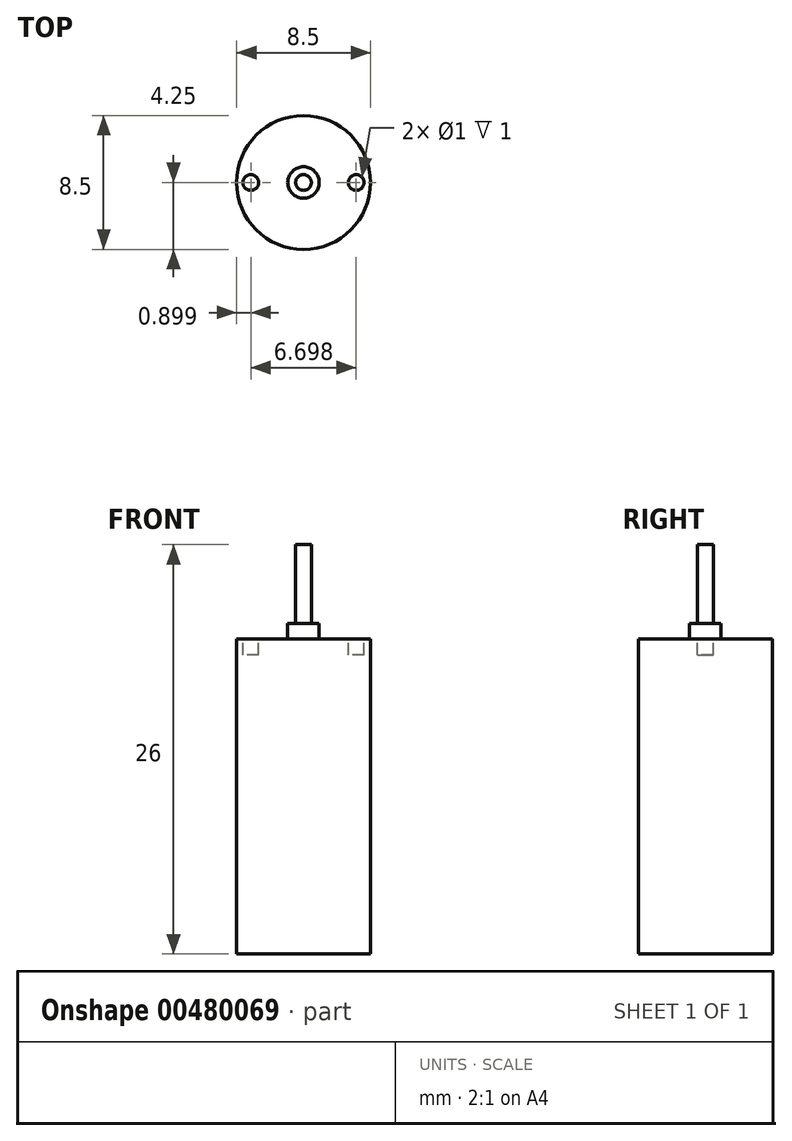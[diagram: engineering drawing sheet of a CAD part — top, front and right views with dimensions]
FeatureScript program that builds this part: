
annotation { "Feature Type Name" : "Feature", "Feature Type Description" : "" }
export const myFeature = defineFeature(function(context is Context, id is Id, definition is map)
    precondition{}
    {
        {
            var Q0;
            Q0=qCreatedBy(makeId("Front.planeOp"),FACE);
            var sketch = newSketch(context, id + "F0", { "sketchPlane" : qUnion([Q0])});
            skLineSegment(sketch, "E0.bottom", {"start": v(-4.64, 12.4) * mm, "end": v(3.86, 12.4) * mm});
            skLineSegment(sketch, "E0.top", {"start": v(-4.64, -7.6) * mm, "end": v(3.86, -7.6) * mm});
            skLineSegment(sketch, "E0.left", {"start": v(-4.64, 12.4) * mm, "end": v(-4.64, -7.6) * mm, "construction": true});
            skLineSegment(sketch, "E0.right", {"start": v(3.86, 12.4) * mm, "end": v(3.86, -7.6) * mm});
            skLineSegment(sketch, "E1.bottom", {"start": v(-0.4, 12.4) * mm, "end": v(-1.4, 12.4) * mm});
            skLineSegment(sketch, "E1.top", {"start": v(-0.4, 13.4) * mm, "end": v(-1.4, 13.4) * mm, "construction": true});
            skLineSegment(sketch, "E1.left", {"start": v(-0.4, 12.4) * mm, "end": v(-0.4, 13.4) * mm});
            skLineSegment(sketch, "E1.right", {"start": v(-1.4, 12.4) * mm, "end": v(-1.4, 13.4) * mm, "construction": true});
            skLineSegment(sketch, "E2", {"start": v(-0.4, -7.6) * mm, "end": v(-0.4, 29.98) * mm, "construction": true});
            skLineSegment(sketch, "E3.bottom", {"start": v(-0.4, 13.4) * mm, "end": v(-0.9, 13.4) * mm});
            skLineSegment(sketch, "E3.top", {"start": v(-0.4, 18.4) * mm, "end": v(-0.9, 18.4) * mm});
            skLineSegment(sketch, "E3.left", {"start": v(-0.4, 13.4) * mm, "end": v(-0.4, 18.4) * mm});
            skLineSegment(sketch, "E3.right", {"start": v(-0.9, 13.4) * mm, "end": v(-0.9, 18.4) * mm, "construction": true});
            skLineSegment(sketch, "E4.MirrorCS", {"start": v(0.6, 12.4) * mm, "end": v(0.6, 13.4) * mm});
            skLineSegment(sketch, "E5.MirrorCS", {"start": v(-0.4, 13.4) * mm, "end": v(0.1, 13.4) * mm});
            skLineSegment(sketch, "E6.MirrorCS", {"start": v(-0.4, 13.4) * mm, "end": v(0.6, 13.4) * mm});
            skLineSegment(sketch, "E7.MirrorCS", {"start": v(0.1, 13.4) * mm, "end": v(0.1, 18.4) * mm});
            skLineSegment(sketch, "E8.MirrorCS", {"start": v(-0.4, 18.4) * mm, "end": v(0.1, 18.4) * mm});
            skLineSegment(sketch, "E9", {"start": v(-0.4, 12.4) * mm, "end": v(-0.4, -7.6) * mm});
            skSolve(sketch);
        }
        {
            var Q0;
            {var subQ0=sQuery(id+"F0.wireOp",EDGE,"E0.right");Q0=makeQuery(id+"F0.imprint","IMPRINT",FACE,{"disambiguationData":[TD([[makeQuery(id+"F0.imprint","IMPRINT",EDGE,{"derivedFrom":subQ0}),-1.0]])]});}
            var Q1;
            {var subQ0=sQuery(id+"F0.wireOp",EDGE,"E1.left");Q1=makeQuery(id+"F0.imprint","IMPRINT",FACE,{"disambiguationData":[TD([[makeQuery(id+"F0.imprint","IMPRINT",EDGE,{"derivedFrom":subQ0}),-1.0]])]});}
            var Q2;
            Q2=makeQuery(id+"F0.imprint","IMPRINT",FACE,{"disambiguationData":[TD([[makeQuery(id+"F0.imprint","IMPRINT",EDGE,{"derivedFrom":sQuery(id+"F0.wireOp",EDGE,"E3.left")}),-1.0]])]});
            var Q3;
            Q3=sQuery(id+"F0.wireOp",EDGE,"E2");
            revolve(context, id + "F1", {"entities" : qUnion([Q0, Q1, Q2]), "axis" : qUnion([Q3]), "revolveType" : RevolveType.FULL});
        }
        {
            var Q0;
            Q0=makeQuery(id+"F1.opRevolve","SWEPT_FACE",FACE,{"disambiguationData":[OSD([sQuery(id+"F0.wireOp",EDGE,"E0.bottom")])]});
            var sketch = newSketch(context, id + "F2", { "sketchPlane" : qUnion([Q0])});
            skLineSegment(sketch, "E10", {"start": v(-9.07, 0) * mm, "end": v(9.62, 0) * mm, "construction": true});
            skLineSegment(sketch, "E11", {"start": v(-0.4, 0) * mm, "end": v(-0.4, 8.75) * mm, "construction": true});
            skLineSegment(sketch, "E12", {"start": v(-0.4, 0) * mm, "end": v(-0.4, -9.34) * mm, "construction": true});
            skLineSegment(sketch, "E13", {"start": v(-4.64, 0) * mm, "end": v(-1.4, 0) * mm});
            skCircle(sketch, "E14", {"center": v(-3.74, 0) * mm, "radius": 0.5 * mm});
            skCircle(sketch, "E15.MirrorC", {"center": v(2.96, 0) * mm, "radius": 0.5 * mm});
            skSolve(sketch);
        }
        {
            var Q0;
            Q0=qSketchRegion(id+"F2",true);
            extrude(context, id + "F3", {"entities" : qUnion([Q0]), "operationType" : NewBodyOperationType.REMOVE, "oppositeDirection" : true, "depth" : 1 * mm});
        }
    });
